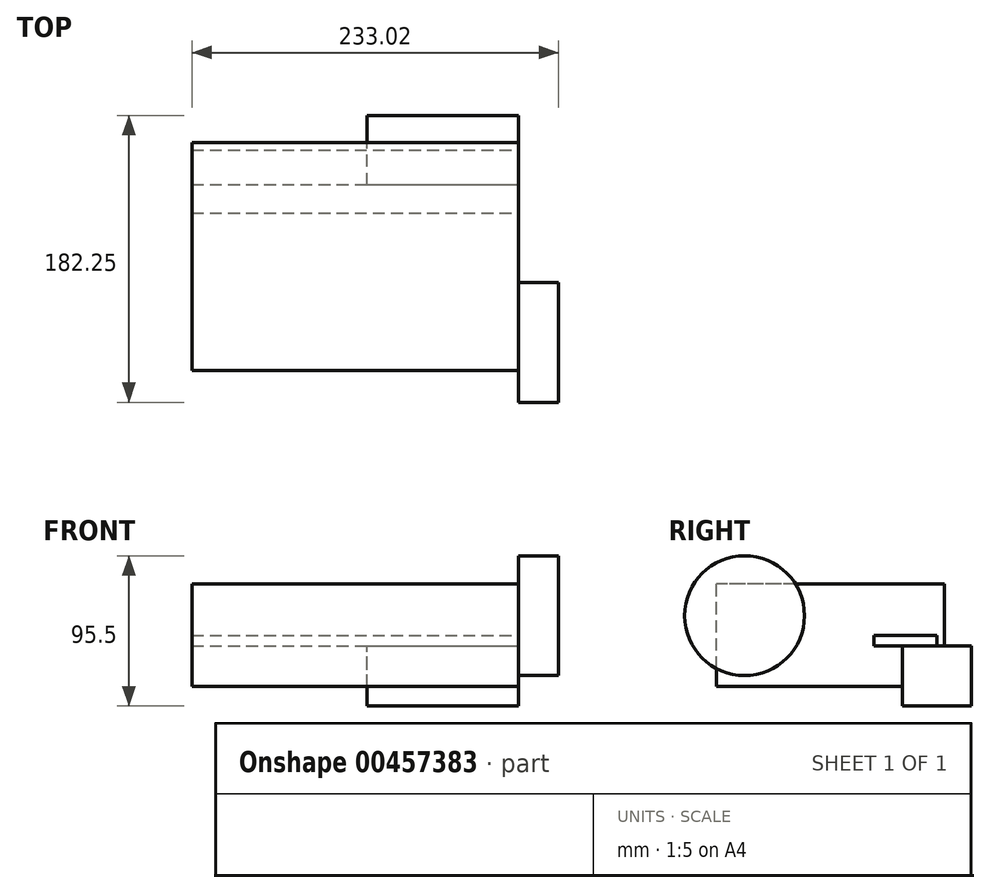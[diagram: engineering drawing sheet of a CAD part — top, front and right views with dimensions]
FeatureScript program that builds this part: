
annotation { "Feature Type Name" : "Feature", "Feature Type Description" : "" }
export const myFeature = defineFeature(function(context is Context, id is Id, definition is map)
    precondition{}
    {
        {
            var Q0;
            Q0=qCreatedBy(makeId("Right.planeOp"),FACE);
            var sketch = newSketch(context, id + "F0", { "sketchPlane" : qUnion([Q0])});
            skCircle(sketch, "E0", {"center": v(-23.95, 0) * mm, "radius": 38.04 * mm});
            skSolve(sketch);
        }
        {
            var Q0;
            Q0=makeQuery(id+"F0.imprint","IMPRINT",FACE,{"disambiguationData":[TD([[makeQuery(id+"F0.imprint","IMPRINT",EDGE,{"derivedFrom":sQuery(id+"F0.wireOp",EDGE,"E0")}),1.0]])]});
            extrude(context, id + "F1", {"entities" : qUnion([Q0]), "depth" : 25.4 * mm});
        }
        {
            var Q0;
            Q0=qCreatedBy(makeId("Right.planeOp"),FACE);
            var sketch = newSketch(context, id + "F2", { "sketchPlane" : qUnion([Q0])});
            skLineSegment(sketch, "E1.bottom", {"start": v(76.26, -57.46) * mm, "end": v(120.25, -57.46) * mm});
            skLineSegment(sketch, "E1.top", {"start": v(76.26, -19.34) * mm, "end": v(120.25, -19.34) * mm});
            skLineSegment(sketch, "E1.left", {"start": v(76.26, -57.46) * mm, "end": v(76.26, -19.34) * mm});
            skLineSegment(sketch, "E1.right", {"start": v(120.25, -57.46) * mm, "end": v(120.25, -19.34) * mm});
            skSolve(sketch);
        }
        {
            var Q0;
            Q0=makeQuery(id+"F2.imprint","IMPRINT",FACE,{"disambiguationData":[TD([[makeQuery(id+"F2.imprint","IMPRINT",EDGE,{"derivedFrom":sQuery(id+"F2.wireOp",EDGE,"E1.bottom")}),1.0]])]});
            extrude(context, id + "F3", {"entities" : qUnion([Q0]), "oppositeDirection" : true, "depth" : 96.47 * mm, "offsetDistance" : 25.4 * mm});
        }
        {
            var Q0;
            Q0=makeQuery(id+"F3.opExtrude","CAP_FACE",FACE,{"disambiguationData":[OSD([sQuery(id+"F2.wireOp",EDGE,"E1.bottom"),sQuery(id+"F2.wireOp",EDGE,"E1.top"),sQuery(id+"F2.wireOp",EDGE,"E1.left"),sQuery(id+"F2.wireOp",EDGE,"E1.right")])],"isStart":true});
            var sketch = newSketch(context, id + "F4", { "sketchPlane" : qUnion([Q0])});
            skLineSegment(sketch, "E2.bottom", {"start": v(103.08, -44.88) * mm, "end": v(-41.73, -44.88) * mm});
            skLineSegment(sketch, "E2.top", {"start": v(103.08, 20.11) * mm, "end": v(-41.73, 20.11) * mm});
            skLineSegment(sketch, "E2.left", {"start": v(103.08, -44.88) * mm, "end": v(103.08, 20.11) * mm});
            skLineSegment(sketch, "E2.right", {"start": v(-41.73, -44.88) * mm, "end": v(-41.73, 20.11) * mm});
            skPoint(sketch, "E3.oppositeSnap0", {"position": v(103.08, -12.38) * mm});
            skLineSegment(sketch, "E3.bottom", {"start": v(98.25, -19.34) * mm, "end": v(58.24, -19.34) * mm});
            skLineSegment(sketch, "E3.top", {"start": v(98.25, -12.38) * mm, "end": v(58.24, -12.38) * mm});
            skLineSegment(sketch, "E3.left", {"start": v(98.25, -19.34) * mm, "end": v(98.25, -12.38) * mm});
            skLineSegment(sketch, "E3.right", {"start": v(58.24, -19.34) * mm, "end": v(58.24, -12.38) * mm});
            skSolve(sketch);
        }
        {
            var Q0;
            {var subQ7=sQuery(id+"F4.wireOp",EDGE,"E2.top");Q0=makeQuery(id+"F4.imprint","IMPRINT",FACE,{"disambiguationData":[TD([[makeQuery(id+"F4.imprint","IMPRINT",EDGE,{"derivedFrom":subQ7}),1.0]])]});}
            extrude(context, id + "F5", {"entities" : qUnion([Q0]), "oppositeDirection" : true, "depth" : 207.62 * mm, "offsetDistance" : 25.4 * mm});
        }
    });
